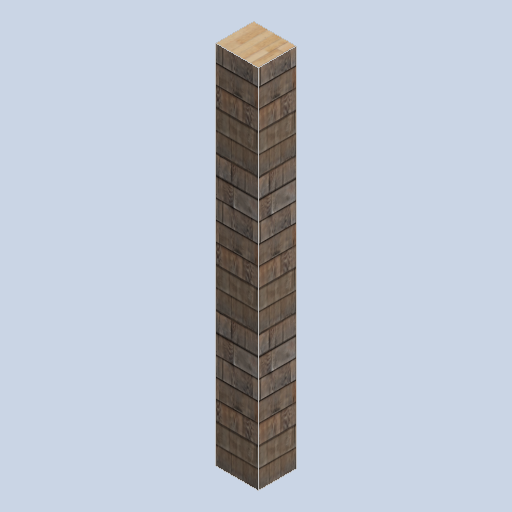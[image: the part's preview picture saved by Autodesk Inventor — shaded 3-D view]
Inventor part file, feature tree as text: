
AUTODESK INVENTOR PART (.ipt)
format: ipt  version: 2024.2 (Build 282272000, 272)  size: 167,936 bytes
history: native  units: in
note: dims shown in document units (in); Inventor stores cm internally (conversion verified against a paired STEP export)
features: other x3, sketch x1
ambient origin geometry x8: Origin, YZ Plane, XZ Plane, XY Plane, X Axis, Y Axis, Z Axis, Center Point
bodies: Solid1 (feature_tree)
feature tree (4):
  other  "support_column_01.ipt"
  other  "Solid1::support_column_01.ipt"
  other  "TaggingFeature1"
  sketch  "Sketch1"  dims[d0=0.3937in]
